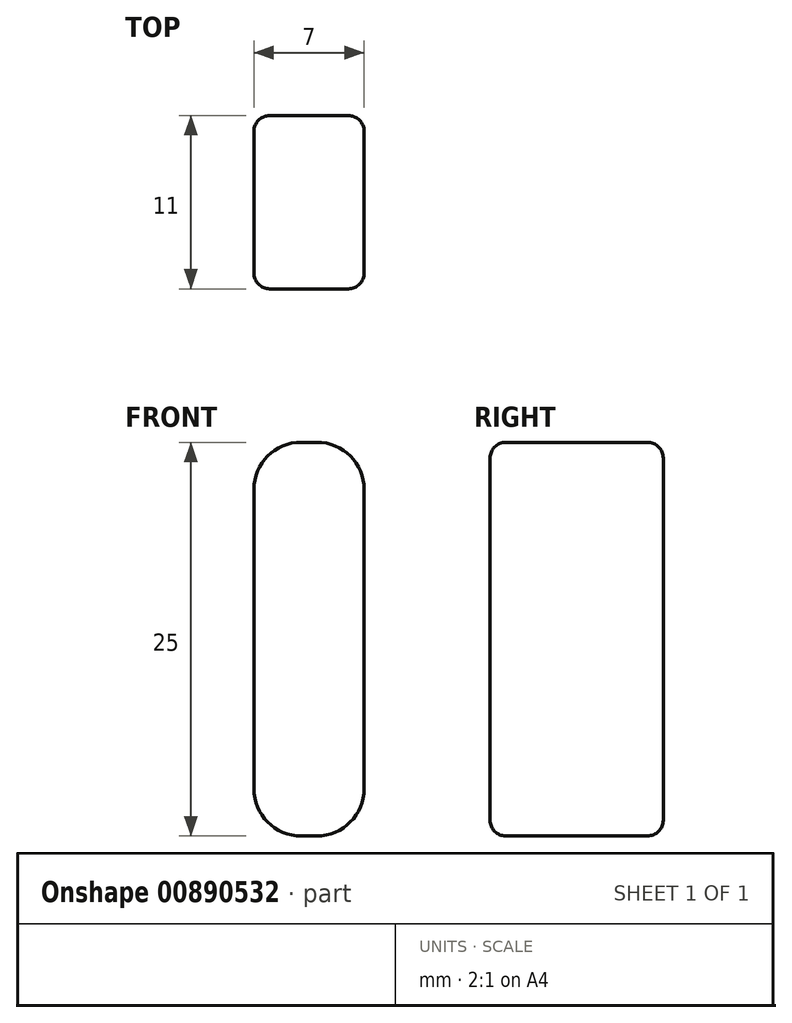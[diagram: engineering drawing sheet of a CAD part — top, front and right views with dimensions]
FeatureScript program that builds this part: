
annotation { "Feature Type Name" : "Feature", "Feature Type Description" : "" }
export const myFeature = defineFeature(function(context is Context, id is Id, definition is map)
    precondition{}
    {
        {
            var Q0;
            Q0=qCreatedBy(makeId("Front.planeOp"),FACE);
            var sketch = newSketch(context, id + "F0", { "sketchPlane" : qUnion([Q0])});
            skLineSegment(sketch, "E0.bottom", {"start": v(3.5, -12.5) * mm, "end": v(-3.5, -12.5) * mm});
            skLineSegment(sketch, "E0.top", {"start": v(3.5, 12.5) * mm, "end": v(-3.5, 12.5) * mm});
            skLineSegment(sketch, "E0.left", {"start": v(3.5, -12.5) * mm, "end": v(3.5, 12.5) * mm});
            skLineSegment(sketch, "E0.right", {"start": v(-3.5, -12.5) * mm, "end": v(-3.5, 12.5) * mm});
            skPoint(sketch, "E0.middle", {"position": v(0, 0) * mm});
            skSolve(sketch);
        }
        {
            var Q0;
            Q0 = qSketchRegion(id + "F0", true);
            extrude(context, id + "F1", {"entities" : qUnion([Q0]), "endBound" : BoundingType.SYMMETRIC, "depth" : 11 * mm, "offsetDistance" : 25 * mm});
        }
        {
            var Q0;
            Q0=makeQuery(id+"F1.opExtrude","SWEPT_EDGE",EDGE,{"disambiguationData":[OSD([sQuery(id+"F0.wireOp",EDGE,"E0.top"),sQuery(id+"F0.wireOp",EDGE,"E0.left")])]});
            var Q1;
            Q1=makeQuery(id+"F1.opExtrude","SWEPT_EDGE",EDGE,{"disambiguationData":[OSD([sQuery(id+"F0.wireOp",EDGE,"E0.top"),sQuery(id+"F0.wireOp",EDGE,"E0.right")])]});
            var Q2;
            Q2=makeQuery(id+"F1.opExtrude","SWEPT_EDGE",EDGE,{"disambiguationData":[OSD([sQuery(id+"F0.wireOp",EDGE,"E0.bottom"),sQuery(id+"F0.wireOp",EDGE,"E0.left")])]});
            var Q3;
            Q3=makeQuery(id+"F1.opExtrude","SWEPT_EDGE",EDGE,{"disambiguationData":[OSD([sQuery(id+"F0.wireOp",EDGE,"E0.bottom"),sQuery(id+"F0.wireOp",EDGE,"E0.right")])]});
            fillet(context, id + "F2", {"entities" : qUnion([Q0, Q1, Q2, Q3]), "radius" : 3 * mm, "tangentPropagation" : true, "allowEdgeOverflow" : false});
        }
        {
            var Q0;
            Q0=makeQuery(id+"F1.opExtrude","CAP_EDGE",EDGE,{"disambiguationData":[OSD([sQuery(id+"F0.wireOp",EDGE,"E0.right")])],"isStart":false});
            var Q1;
            Q1=makeQuery(id+"F1.opExtrude","CAP_EDGE",EDGE,{"disambiguationData":[OSD([sQuery(id+"F0.wireOp",EDGE,"E0.left")])],"isStart":false});
            var Q2;
            {var subQ0=sQuery(id+"F0.wireOp",EDGE,"E0.right");var subQ1=sQuery(id+"F0.wireOp",EDGE,"E0.bottom");Q2=makeQuery(id+"F2.opFillet","BLEND_EDGE",EDGE,{"blendedFrom":[makeQuery(id+"F1.opExtrude","SWEPT_EDGE",EDGE,{"disambiguationData":[OSD([subQ1,subQ0])]}),makeQuery(id+"F1.opExtrude","CAP_FACE",FACE,{"disambiguationData":[OSD([subQ1,sQuery(id+"F0.wireOp",EDGE,"E0.top"),sQuery(id+"F0.wireOp",EDGE,"E0.left"),subQ0])],"isStart":false})],"blendedInto":[makeQuery(id+"F1.opExtrude","CAP_FACE",FACE,{"disambiguationData":[OSD([subQ1,sQuery(id+"F0.wireOp",EDGE,"E0.top"),sQuery(id+"F0.wireOp",EDGE,"E0.left"),subQ0])],"isStart":false})]});}
            var Q3;
            {var subQ0=sQuery(id+"F0.wireOp",EDGE,"E0.left");var subQ1=sQuery(id+"F0.wireOp",EDGE,"E0.top");Q3=makeQuery(id+"F2.opFillet","BLEND_EDGE",EDGE,{"blendedFrom":[makeQuery(id+"F1.opExtrude","SWEPT_EDGE",EDGE,{"disambiguationData":[OSD([subQ1,subQ0])]}),makeQuery(id+"F1.opExtrude","CAP_FACE",FACE,{"disambiguationData":[OSD([sQuery(id+"F0.wireOp",EDGE,"E0.bottom"),subQ1,subQ0,sQuery(id+"F0.wireOp",EDGE,"E0.right")])],"isStart":false})],"blendedInto":[makeQuery(id+"F1.opExtrude","CAP_FACE",FACE,{"disambiguationData":[OSD([sQuery(id+"F0.wireOp",EDGE,"E0.bottom"),subQ1,subQ0,sQuery(id+"F0.wireOp",EDGE,"E0.right")])],"isStart":false})]});}
            var Q4;
            Q4=makeQuery(id+"F1.opExtrude","CAP_EDGE",EDGE,{"disambiguationData":[OSD([sQuery(id+"F0.wireOp",EDGE,"E0.bottom")])],"isStart":false});
            var Q5;
            {var subQ0=sQuery(id+"F0.wireOp",EDGE,"E0.right");var subQ1=sQuery(id+"F0.wireOp",EDGE,"E0.top");Q5=makeQuery(id+"F2.opFillet","BLEND_EDGE",EDGE,{"blendedFrom":[makeQuery(id+"F1.opExtrude","SWEPT_EDGE",EDGE,{"disambiguationData":[OSD([subQ1,subQ0])]}),makeQuery(id+"F1.opExtrude","CAP_FACE",FACE,{"disambiguationData":[OSD([sQuery(id+"F0.wireOp",EDGE,"E0.bottom"),subQ1,sQuery(id+"F0.wireOp",EDGE,"E0.left"),subQ0])],"isStart":false})],"blendedInto":[makeQuery(id+"F1.opExtrude","CAP_FACE",FACE,{"disambiguationData":[OSD([sQuery(id+"F0.wireOp",EDGE,"E0.bottom"),subQ1,sQuery(id+"F0.wireOp",EDGE,"E0.left"),subQ0])],"isStart":false})]});}
            var Q6;
            Q6=makeQuery(id+"F1.opExtrude","CAP_EDGE",EDGE,{"disambiguationData":[OSD([sQuery(id+"F0.wireOp",EDGE,"E0.top")])],"isStart":false});
            var Q7;
            Q7=makeQuery(id+"F1.opExtrude","CAP_EDGE",EDGE,{"disambiguationData":[OSD([sQuery(id+"F0.wireOp",EDGE,"E0.left")])],"isStart":true});
            var Q8;
            Q8=makeQuery(id+"F1.opExtrude","CAP_EDGE",EDGE,{"disambiguationData":[OSD([sQuery(id+"F0.wireOp",EDGE,"E0.right")])],"isStart":true});
            var Q9;
            Q9=makeQuery(id+"F1.opExtrude","CAP_FACE",FACE,{"disambiguationData":[OSD([sQuery(id+"F0.wireOp",EDGE,"E0.bottom"),sQuery(id+"F0.wireOp",EDGE,"E0.top"),sQuery(id+"F0.wireOp",EDGE,"E0.left"),sQuery(id+"F0.wireOp",EDGE,"E0.right")])],"isStart":true});
            fillet(context, id + "F3", {"entities" : qUnion([Q0, Q1, Q2, Q3, Q4, Q5, Q6, Q7, Q8, Q9]), "radius" : 1 * mm, "tangentPropagation" : true, "allowEdgeOverflow" : false});
        }
    });
